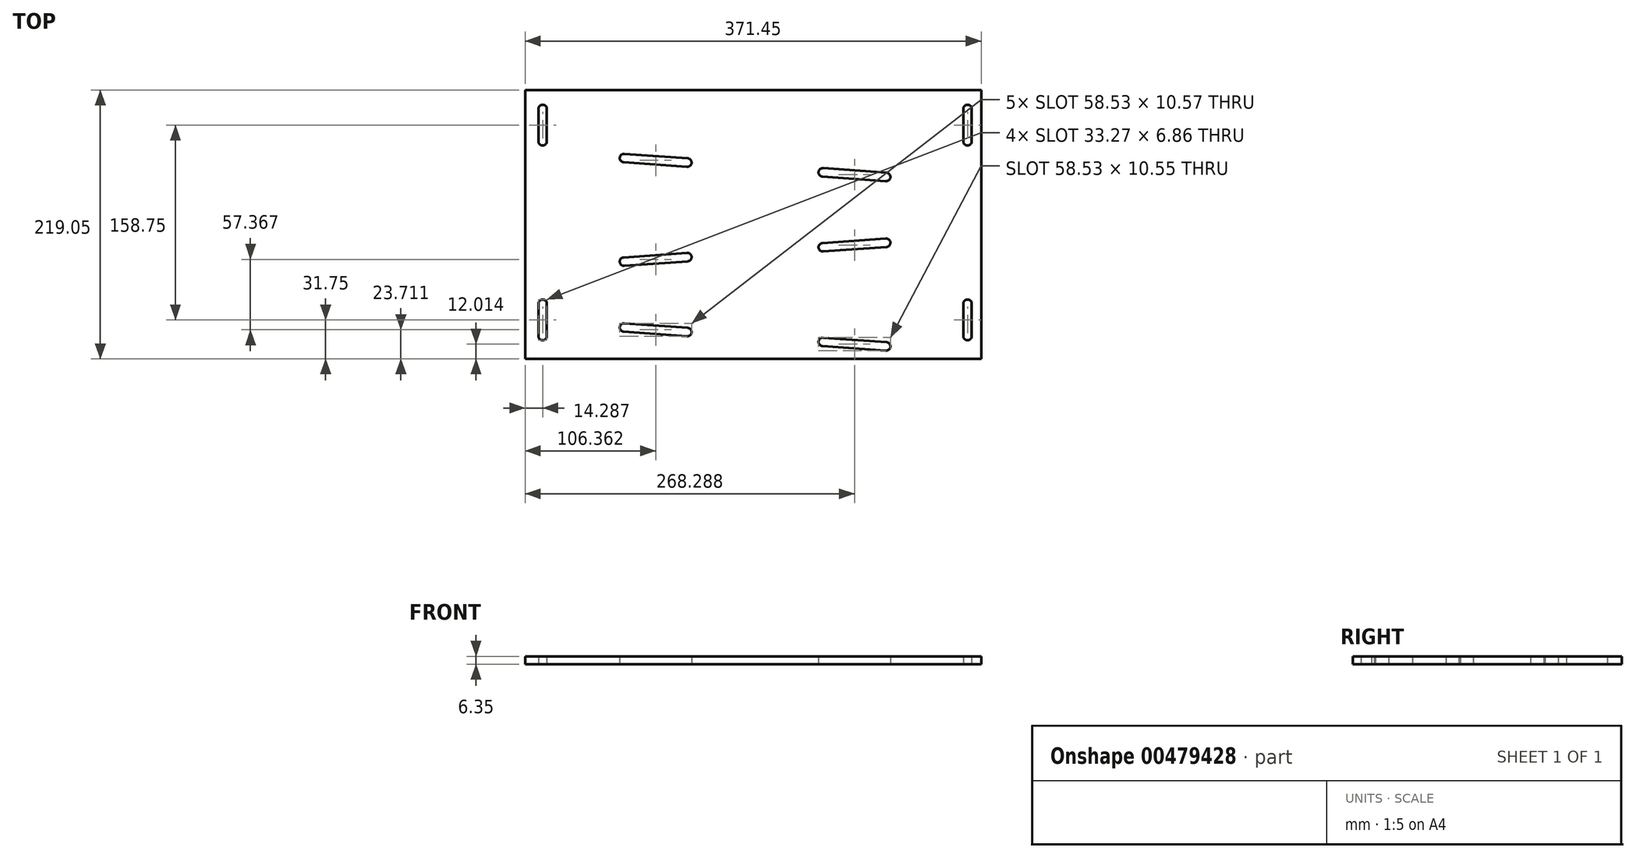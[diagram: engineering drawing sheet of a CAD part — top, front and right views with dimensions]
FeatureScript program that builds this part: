
annotation { "Feature Type Name" : "Feature", "Feature Type Description" : "" }
export const myFeature = defineFeature(function(context is Context, id is Id, definition is map)
    precondition{}
    {
        {
            var Q0;
            Q0=qCreatedBy(makeId("Top.planeOp"),FACE);
            var sketch = newSketch(context, id + "F0", { "sketchPlane" : qUnion([Q0]), "disableImprinting" : false});
            skLineSegment(sketch, "E0.bottom", {"start": v(0, 0) * mm, "end": v(371.45, 0) * mm});
            skLineSegment(sketch, "E0.top", {"start": v(0, 219.05) * mm, "end": v(371.45, 219.05) * mm});
            skLineSegment(sketch, "E0.left", {"start": v(0, 0) * mm, "end": v(0, 219.05) * mm});
            skLineSegment(sketch, "E0.right", {"start": v(371.45, 0) * mm, "end": v(371.45, 219.05) * mm});
            skCircle(sketch, "E1", {"center": v(14.29, 203.7) * mm, "radius": 3.43 * mm});
            skCircle(sketch, "E2", {"center": v(14.29, 44.96) * mm, "radius": 3.43 * mm});
            skCircle(sketch, "E3", {"center": v(14.29, 177.3) * mm, "radius": 3.43 * mm});
            skCircle(sketch, "E4", {"center": v(14.29, 18.54) * mm, "radius": 3.43 * mm});
            skCircle(sketch, "E5", {"center": v(80.52, 25.58) * mm, "radius": 3.43 * mm});
            skCircle(sketch, "E6", {"center": v(80.52, 79.21) * mm, "radius": 3.43 * mm});
            skCircle(sketch, "E7", {"center": v(80.52, 163.7) * mm, "radius": 3.43 * mm});
            skCircle(sketch, "E8", {"center": v(132.2, 159.97) * mm, "radius": 3.43 * mm});
            skCircle(sketch, "E9", {"center": v(132.2, 82.94) * mm, "radius": 3.43 * mm});
            skCircle(sketch, "E10", {"center": v(132.2, 21.84) * mm, "radius": 3.43 * mm});
            skCircle(sketch, "E11", {"center": v(242.44, 152) * mm, "radius": 3.43 * mm});
            skCircle(sketch, "E12", {"center": v(242.44, 13.87) * mm, "radius": 3.43 * mm});
            skCircle(sketch, "E13", {"center": v(242.44, 90.9) * mm, "radius": 3.43 * mm});
            skCircle(sketch, "E14", {"center": v(294.13, 10.16) * mm, "radius": 3.43 * mm});
            skCircle(sketch, "E15", {"center": v(294.13, 148.27) * mm, "radius": 3.43 * mm});
            skCircle(sketch, "E16", {"center": v(294.13, 94.63) * mm, "radius": 3.43 * mm});
            skCircle(sketch, "E17", {"center": v(360.38, 18.54) * mm, "radius": 3.43 * mm});
            skCircle(sketch, "E18", {"center": v(360.38, 203.7) * mm, "radius": 3.43 * mm});
            skCircle(sketch, "E19", {"center": v(360.38, 44.96) * mm, "radius": 3.43 * mm});
            skCircle(sketch, "E20", {"center": v(360.38, 177.3) * mm, "radius": 3.43 * mm});
            skLineSegment(sketch, "E21", {"start": v(17.72, 203.7) * mm, "end": v(17.72, 177.3) * mm});
            skLineSegment(sketch, "E22", {"start": v(10.86, 203.7) * mm, "end": v(10.86, 177.3) * mm});
            skLineSegment(sketch, "E23", {"start": v(80.76, 167.12) * mm, "end": v(132.45, 163.39) * mm});
            skLineSegment(sketch, "E24", {"start": v(80.27, 160.28) * mm, "end": v(131.96, 156.55) * mm});
            skLineSegment(sketch, "E25", {"start": v(242.69, 155.43) * mm, "end": v(294.38, 151.7) * mm});
            skLineSegment(sketch, "E26", {"start": v(242.2, 148.59) * mm, "end": v(293.89, 144.85) * mm});
            skLineSegment(sketch, "E27", {"start": v(356.95, 203.7) * mm, "end": v(356.95, 177.3) * mm});
            skLineSegment(sketch, "E28", {"start": v(363.8, 203.7) * mm, "end": v(363.8, 177.3) * mm});
            skLineSegment(sketch, "E29", {"start": v(242.2, 94.32) * mm, "end": v(293.89, 98.05) * mm});
            skLineSegment(sketch, "E30", {"start": v(242.69, 87.48) * mm, "end": v(294.38, 91.21) * mm});
            skLineSegment(sketch, "E31", {"start": v(80.76, 75.8) * mm, "end": v(132.45, 79.52) * mm});
            skLineSegment(sketch, "E32", {"start": v(80.27, 82.63) * mm, "end": v(131.96, 86.36) * mm});
            skLineSegment(sketch, "E33", {"start": v(17.72, 44.96) * mm, "end": v(17.72, 18.54) * mm});
            skLineSegment(sketch, "E34", {"start": v(10.86, 44.96) * mm, "end": v(10.86, 18.54) * mm});
            skLineSegment(sketch, "E35", {"start": v(80.77, 29) * mm, "end": v(132.45, 25.26) * mm});
            skLineSegment(sketch, "E36", {"start": v(80.27, 22.16) * mm, "end": v(131.96, 18.42) * mm});
            skLineSegment(sketch, "E37", {"start": v(242.69, 17.29) * mm, "end": v(294.38, 13.58) * mm});
            skLineSegment(sketch, "E38", {"start": v(242.2, 10.45) * mm, "end": v(293.89, 6.74) * mm});
            skLineSegment(sketch, "E39", {"start": v(356.95, 44.96) * mm, "end": v(356.95, 18.54) * mm});
            skLineSegment(sketch, "E40", {"start": v(363.8, 44.96) * mm, "end": v(363.8, 18.54) * mm});
            skSolve(sketch);
        }
        {
            var Q0;
            Q0 = qSketchRegion(id + "F0", true);
            extrude(context, id + "F1", {"entities" : qUnion([Q0]), "depth" : 6.35 * mm, "offsetDistance" : 25.4 * mm});
        }
    });
